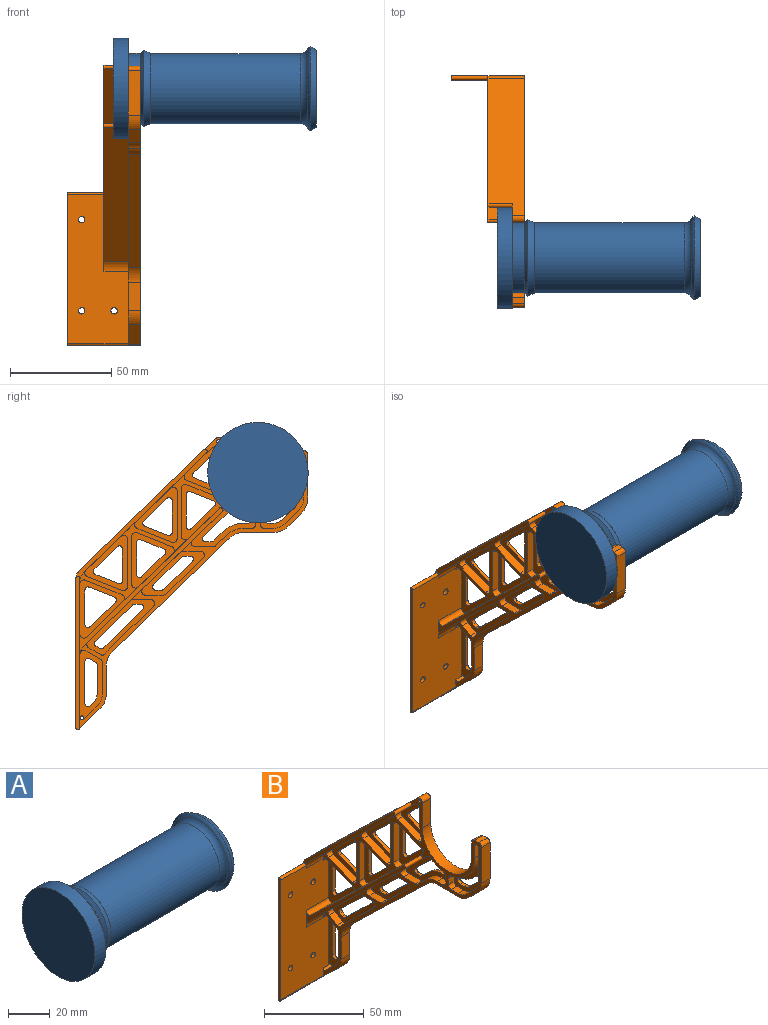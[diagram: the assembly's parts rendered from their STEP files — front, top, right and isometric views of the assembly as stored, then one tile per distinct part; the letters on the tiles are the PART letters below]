
ASSEMBLY  parts=2 mates=1
PART A: 12 faces, bbox 100.4x49.6x49.6 mm
  f0: cylinder r=17.3mm len=74.07mm, axis (-1,0,0), area 8051.5mm2, adj f1,f9
  f1: plane 34.94x34.94mm, normal (1,0,0), area 18.7mm2, adj f0,f10
  f2: cone r=17.3mm half-angle=45deg, axis (1,0,0), area 254.9mm2, adj f3,f10
  f3: cylinder r=17.3mm len=34.6mm, axis (-1,0,0), area 641.3mm2, adj f2,f4
  f4: plane 49.6x49.6mm, normal (1,0,0), area 992mm2, adj f3,f5
  f5: cylinder r=24.8mm len=49.6mm, axis (-1,0,0), area 1168.7mm2, adj f4,f6
  f6: plane 49.6x49.6mm, normal (-1,0,0), area 1932.2mm2, adj f5
  f7: plane 38.06x38.06mm, normal (1,0,0), area 1137.9mm2, adj f11
  f8: torus R=17.3mm, axis (-1,0,0), area 264.5mm2, adj f9,f11
  f9: torus R=21.3mm, axis (-1,0,0), area 473.5mm2, adj f0,f8
  f10: cone r=18.89mm half-angle=22.5deg, axis (-1,0,0), area 422.1mm2, adj f1,f2
  f11: cone r=20.76mm half-angle=30deg, axis (-1,0,0), area 433.1mm2, adj f7,f8
PART B: 211 faces, bbox 36x114.5x144.3 mm
  f0: plane 35.01x21.5mm, normal (-1,0,0), area 200.1mm2, adj f6,f11,f85,f86,f87,f88,f89,f96
  f1: plane 34.13x11.1mm, normal (-1,0,0), area 178.3mm2, adj f2,f28,f92,f93,f94,f95,f108,f122
  f2: cylinder r=7mm len=16mm, axis (1,0,0), area 69.8mm2, adj f1,f24,f25,f28,f36,f122
  f3: cylinder r=12mm len=4mm, axis (1,0,0), area 11.5mm2, adj f9,f10,f24,f124
  f4: plane 31.92x21.51mm, normal (-1,0,0), area 193.4mm2, adj f5,f25,f39,f82,f90,f91,f104,f105
  f5: plane 4.1x4mm, normal (0,0,1), area 16.4mm2, adj f4,f24,f90,f110
  f6: cylinder r=19.5mm len=19.31mm, axis (1,0,0), area 111.6mm2, adj f0,f11,f24,f112
  f7: plane 31x21.82mm, normal (-1,0,0), area 188.1mm2, adj f8,f25,f102,f103,f113,f114,f119,f120
  f8: plane 18.38x17.82mm, normal (0,0.7,0.72), area 102.4mm2, adj f7,f24,f114,f119
  f9: plane 33.53x27.62mm, normal (-1,0,0), area 210.3mm2, adj f3,f10,f25,f101,f107,f117,f118,f121
  f10: plane 21.68x21.02mm, normal (0,0.7,0.72), area 120.8mm2, adj f3,f9,f24,f118
  f11: plane 7.51x4mm, normal (0,-1,0), area 30mm2, adj f0,f6,f24,f96
  f12: plane 27.39x21.13mm, normal (-1,0,0), area 180.4mm2, adj f18,f53,f54,f75,f76,f77,f149,f150
  f13: plane 27.39x21.13mm, normal (-1,0,0), area 180.4mm2, adj f17,f50,f51,f70,f71,f72,f165,f166
  f14: plane 27.39x21.13mm, normal (-1,0,0), area 180.4mm2, adj f17,f48,f49,f67,f68,f69,f156,f157
  f15: plane 28.75x22.13mm, normal (-1,0,0), area 190mm2, adj f17,f28,f47,f63,f66,f84,f146,f147
  f16: plane 22.35x18.45mm, normal (-1,0,0), area 147.4mm2, adj f18,f40,f41,f52,f73,f74,f83,f168
  f17: plane 67.2x65.14mm, normal (0,0.7,0.72), area 1387.2mm2, adj f13,f14,f15,f24,f36,f66,f67,f69
  f18: plane 62.98x61.06mm, normal (0,-0.7,-0.72), area 1275.8mm2, adj f12,f16,f24,f29,f35,f62,f64,f74
  f19: plane 144.33x114.5mm, normal (1,0,0), area 3611.6mm2, adj f20,f21,f22,f23,f26,f34,f37,f38
  f20: plane 10.26x9.95mm, normal (0,-0.7,-0.72), area 85.8mm2, adj f19,f24,f57,f100
  f21: plane 6.65x6.45mm, normal (0,-0.7,-0.72), area 55.6mm2, adj f19,f24,f58,f61
  f22: plane 22.06x6mm, normal (0,-1,0), area 132.4mm2, adj f19,f24,f61,f79
  f23: plane 9.01x6mm, normal (0,1,0), area 54mm2, adj f19,f24,f38,f80
  f24: plane 144.05x112.8mm, normal (-1,0,0), area 1051mm2, adj f2,f3,f5,f6,f8,f10,f11,f17
  f25: plane 71.62x69.43mm, normal (0,-0.7,-0.72), area 1459.2mm2, adj f2,f4,f7,f9,f24,f36,f82,f98
  f26: plane 73.65x36mm, normal (0,1,0), area 2619.3mm2, adj f19,f27,f30,f31,f32,f33,f56,f99
  f27: plane 75.65x2mm, normal (-1,0,0), area 150.4mm2, adj f26,f28,f99,f100
  f28: plane 73.65x34mm, normal (0,-1,0), area 2254.3mm2, adj f1,f2,f15,f24,f27,f30,f31,f32
  f29: plane 27.39x21.13mm, normal (-1,0,0), area 180.4mm2, adj f18,f46,f55,f64,f65,f78,f125,f126
  f30: cylinder r=1.6mm len=3.2mm, axis (0,-1,0), area 20.1mm2, adj f26,f28
  f31: cylinder r=1.6mm len=3.2mm, axis (0,-1,0), area 20.1mm2, adj f26,f28
  f32: cylinder r=1.6mm len=3.2mm, axis (0,-1,0), area 20.1mm2, adj f26,f28
  f33: cylinder r=1.6mm len=3.2mm, axis (0,-1,0), area 20.1mm2, adj f26,f28
  f34: plane 67.59x65.52mm, normal (0,0.7,0.72), area 1597.4mm2, adj f19,f24,f35,f56,f81,f97
  f35: plane 65.46x65mm, normal (-1,0,0), area 179.4mm2, adj f18,f28,f34,f56,f62,f97,f99
  f36: plane 72.85x70.62mm, normal (-1,0,0), area 201.4mm2, adj f2,f17,f25,f28,f84,f98
  f37: plane 15.4x6mm, normal (0,-1,0), area 92.4mm2, adj f19,f24,f38,f81
  f38: cylinder r=17.5mm len=35mm, axis (1,0,0), area 329.9mm2, adj f19,f23,f24,f37
  f39: cylinder r=19.5mm len=8.95mm, axis (1,0,0), area 39.1mm2, adj f4,f24,f82,f109
  f40: plane 10.68x4mm, normal (0,1,0), area 42.7mm2, adj f16,f24,f41,f83
  f41: cylinder r=19.5mm len=6.96mm, axis (1,0,0), area 28.5mm2, adj f16,f24,f40,f73
  f42: plane 6x3mm, normal (0,0,1), area 18mm2, adj f19,f24,f79,f80
  f43: plane 13.89x6mm, normal (0,-1,0), area 83.3mm2, adj f19,f24,f57,f60
  f44: plane 14.95x6mm, normal (0,0,-1), area 89.7mm2, adj f19,f24,f58,f59
  f45: plane 57.9x56.13mm, normal (0,-0.7,-0.72), area 483.8mm2, adj f19,f24,f59,f60
  f46: plane 17.13x6.78mm, normal (0,-0.37,0.93), area 73.7mm2, adj f24,f29,f64,f65
  f47: plane 18.13x7.18mm, normal (0,0.37,-0.93), area 78mm2, adj f15,f24,f63,f66
  f48: plane 23.39x4mm, normal (0,-1,0), area 93.5mm2, adj f14,f24,f67,f68
  f49: plane 17.13x6.78mm, normal (0,0.37,-0.93), area 73.7mm2, adj f14,f24,f68,f69
  f50: plane 23.39x4mm, normal (0,-1,0), area 93.5mm2, adj f13,f24,f70,f71
  f51: plane 17.13x6.78mm, normal (0,0.37,-0.93), area 73.7mm2, adj f13,f24,f71,f72
  f52: plane 14.45x5.72mm, normal (0,-0.37,0.93), area 62.1mm2, adj f16,f24,f73,f74
  f53: plane 23.39x4mm, normal (0,1,0), area 93.5mm2, adj f12,f24,f75,f76
  f54: plane 17.13x6.78mm, normal (0,-0.37,0.93), area 73.7mm2, adj f12,f24,f76,f77
  f55: plane 23.39x4mm, normal (0,1,0), area 93.5mm2, adj f24,f29,f65,f78
  f56: cylinder r=5mm len=18mm, axis (-1,0,0), area 72.1mm2, adj f19,f26,f34,f35
  f57: cylinder r=10mm len=7.18mm, axis (-1,0,0), area 48.1mm2, adj f19,f20,f24,f43
  f58: cylinder r=10mm len=6.96mm, axis (1,0,0), area 46.2mm2, adj f19,f21,f24,f44
  f59: cylinder r=10mm len=6.96mm, axis (1,0,0), area 46.2mm2, adj f19,f24,f44,f45
  f60: cylinder r=10mm len=7.18mm, axis (1,0,0), area 48.1mm2, adj f19,f24,f43,f45
  f61: cylinder r=10mm len=7.18mm, axis (1,0,0), area 48.1mm2, adj f19,f21,f22,f24
  f62: cylinder r=7mm len=12mm, axis (-1,0,0), area 67.3mm2, adj f18,f24,f28,f35
  f63: cylinder r=2mm len=4mm, axis (1,0,0), area 15.6mm2, adj f15,f24,f28,f47
  f64: cylinder r=2mm len=4mm, axis (1,0,0), area 16mm2, adj f18,f24,f29,f46
  f65: cylinder r=2mm len=4mm, axis (-1,0,0), area 15.6mm2, adj f24,f29,f46,f55
  f66: cylinder r=2mm len=4mm, axis (1,0,0), area 16mm2, adj f15,f17,f24,f47
  f67: cylinder r=2mm len=4mm, axis (1,0,0), area 18.7mm2, adj f14,f17,f24,f48
  f68: cylinder r=2mm len=4mm, axis (-1,0,0), area 15.6mm2, adj f14,f24,f48,f49
  f69: cylinder r=2mm len=4mm, axis (1,0,0), area 16mm2, adj f14,f17,f24,f49
  f70: cylinder r=2mm len=4mm, axis (1,0,0), area 18.7mm2, adj f13,f17,f24,f50
  f71: cylinder r=2mm len=4mm, axis (-1,0,0), area 15.6mm2, adj f13,f24,f50,f51
  f72: cylinder r=2mm len=4mm, axis (1,0,0), area 16mm2, adj f13,f17,f24,f51
  f73: cylinder r=2mm len=4mm, axis (1,0,0), area 18.5mm2, adj f16,f24,f41,f52
  f74: cylinder r=2mm len=4mm, axis (-1,0,0), area 16mm2, adj f16,f18,f24,f52
  f75: cylinder r=2mm len=4mm, axis (-1,0,0), area 18.7mm2, adj f12,f18,f24,f53
  f76: cylinder r=2mm len=4mm, axis (-1,0,0), area 15.6mm2, adj f12,f24,f53,f54
  f77: cylinder r=2mm len=4mm, axis (-1,0,0), area 16mm2, adj f12,f18,f24,f54
  f78: cylinder r=2mm len=4mm, axis (-1,0,0), area 18.7mm2, adj f18,f24,f29,f55
  f79: cylinder r=2mm len=6mm, axis (-1,0,0), area 18.8mm2, adj f19,f22,f24,f42
  f80: cylinder r=2mm len=6mm, axis (1,0,0), area 18.8mm2, adj f19,f23,f24,f42
  f81: cylinder r=2mm len=6mm, axis (-1,0,0), area 28.1mm2, adj f19,f24,f34,f37
  f82: cylinder r=2mm len=4mm, axis (1,0,0), area 11.3mm2, adj f4,f24,f25,f39
  f83: cylinder r=2mm len=4mm, axis (-1,0,0), area 18.7mm2, adj f16,f18,f24,f40
  f84: cylinder r=2mm len=16mm, axis (-1,0,0), area 74.9mm2, adj f15,f17,f28,f36
  f85: plane 20.56x4mm, normal (0,1,0), area 82.2mm2, adj f0,f24,f86,f96
  f86: cylinder r=8mm len=5.74mm, axis (1,0,0), area 25.6mm2, adj f0,f24,f85,f87
  f87: plane 6.65x6.45mm, normal (0,0.7,0.72), area 37mm2, adj f0,f24,f86,f88
  f88: cylinder r=8mm len=5.57mm, axis (1,0,0), area 24.6mm2, adj f0,f24,f87,f89
  f89: plane 4.85x4mm, normal (0,0,1), area 19.4mm2, adj f0,f24,f88,f111
  f90: cylinder r=12mm len=8.35mm, axis (1,0,0), area 37mm2, adj f4,f5,f24,f91
  f91: plane 5.45x5.29mm, normal (0,0.7,0.72), area 30.4mm2, adj f4,f24,f90,f115
  f92: cylinder r=12mm len=4mm, axis (1,0,0), area 5.9mm2, adj f1,f24,f93,f123
  f93: plane 13.89x4mm, normal (0,1,0), area 55.5mm2, adj f1,f24,f92,f94
  f94: cylinder r=8mm len=5.74mm, axis (1,0,0), area 25.6mm2, adj f1,f24,f93,f95
  f95: plane 6.87x6.66mm, normal (0,0.7,0.72), area 38.3mm2, adj f1,f24,f94,f209
  f96: cylinder r=1.5mm len=6mm, axis (1,0,0), area 37.7mm2, adj f0,f11,f19,f24,f85
  f97: cylinder r=1mm len=12mm, axis (-1,0,0), area 37.7mm2, adj f18,f24,f34,f35
  f98: cylinder r=1mm len=12mm, axis (-1,0,0), area 37.7mm2, adj f17,f24,f25,f36
  f99: cylinder r=1mm len=18mm, axis (-1,0,0), area 56.5mm2, adj f26,f27,f28,f35
  f100: cylinder r=1mm len=36mm, axis (1,0,0), area 108.3mm2, adj f19,f20,f24,f26,f27,f28
  f101: plane 8.62x4mm, normal (0,0,-1), area 34.5mm2, adj f9,f24,f117,f118
  f102: plane 8.62x4mm, normal (0,0,1), area 34.5mm2, adj f7,f24,f119,f120
  f103: plane 8.62x4mm, normal (0,0,-1), area 34.5mm2, adj f7,f24,f113,f114
  f104: plane 8.62x4mm, normal (0,0,1), area 34.5mm2, adj f4,f24,f115,f116
  f105: plane 4.21x4mm, normal (0,1,0), area 16.8mm2, adj f4,f24,f109,f110
  f106: plane 4.21x4mm, normal (0,-1,0), area 16.8mm2, adj f0,f24,f111,f112
  f107: plane 5.74x4mm, normal (0,-0.5,0.86), area 26.6mm2, adj f9,f24,f121,f124
  f108: plane 7.08x4.13mm, normal (0,0.5,-0.86), area 32.8mm2, adj f1,f24,f122,f123
  f109: cylinder r=2mm len=4mm, axis (1,0,0), area 11.4mm2, adj f4,f24,f39,f105
  f110: cylinder r=2mm len=4mm, axis (1,0,0), area 12.6mm2, adj f4,f5,f24,f105
  f111: cylinder r=2mm len=4mm, axis (-1,0,0), area 12.6mm2, adj f0,f24,f89,f106
  f112: cylinder r=2mm len=4mm, axis (1,0,0), area 11.4mm2, adj f0,f6,f24,f106
  f113: cylinder r=2mm len=4mm, axis (-1,0,0), area 6.2mm2, adj f7,f24,f25,f103
  f114: cylinder r=2mm len=4mm, axis (1,0,0), area 19mm2, adj f7,f8,f24,f103
  f115: cylinder r=2mm len=4mm, axis (-1,0,0), area 6.2mm2, adj f4,f24,f91,f104
  f116: cylinder r=2mm len=4mm, axis (1,0,0), area 19mm2, adj f4,f24,f25,f104
  f117: cylinder r=2mm len=4mm, axis (-1,0,0), area 6.2mm2, adj f9,f24,f25,f101
  f118: cylinder r=2mm len=4mm, axis (1,0,0), area 19mm2, adj f9,f10,f24,f101
  f119: cylinder r=2mm len=4mm, axis (-1,0,0), area 6.2mm2, adj f7,f8,f24,f102
  f120: cylinder r=2mm len=4mm, axis (1,0,0), area 19mm2, adj f7,f24,f25,f102
  f121: cylinder r=2mm len=4mm, axis (1,0,0), area 14.7mm2, adj f9,f24,f25,f107
  f122: cylinder r=2mm len=4mm, axis (1,0,0), area 16.1mm2, adj f1,f2,f24,f108
  f123: cylinder r=2mm len=4mm, axis (1,0,0), area 9.3mm2, adj f1,f24,f92,f108
  f124: cylinder r=2mm len=4mm, axis (1,0,0), area 12.3mm2, adj f3,f9,f24,f107
  f125: plane 11.51x11.16mm, normal (0,-0.7,-0.72), area 32.1mm2, adj f19,f29,f200,f202
  f126: plane 11.51x4.56mm, normal (0,-0.37,0.93), area 24.8mm2, adj f19,f29,f200,f201
  f127: plane 15.72x2mm, normal (0,1,0), area 31.4mm2, adj f19,f29,f201,f202
  f128: plane 2x0.54mm, normal (0,1,0), area 1.1mm2, adj f4,f19,f188,f192
  f129: cylinder r=22mm len=7.16mm, axis (-1,0,0), area 15.6mm2, adj f4,f19,f188,f189
  f130: plane 13.34x12.93mm, normal (0,-0.7,-0.72), area 37.1mm2, adj f4,f19,f189,f190
  f131: plane 2.87x2mm, normal (0,0,1), area 5.7mm2, adj f4,f19,f190,f191
  f132: plane 4.87x4.72mm, normal (0,0.7,0.72), area 13.6mm2, adj f4,f19,f133,f191
  f133: cylinder r=14.5mm len=10.09mm, axis (-1,0,0), area 22.3mm2, adj f4,f19,f132,f134
  f134: plane 2.1x2mm, normal (0,0,1), area 4.2mm2, adj f4,f19,f133,f192
  f135: plane 2.87x2mm, normal (0,0,-1), area 5.7mm2, adj f9,f19,f184,f187
  f136: plane 18.43x17.87mm, normal (0,-0.7,-0.72), area 51.3mm2, adj f9,f19,f184,f185
  f137: plane 2x1.89mm, normal (0,-0.5,0.86), area 4.4mm2, adj f9,f19,f185,f186
  f138: cylinder r=14.5mm len=2mm, axis (-1,0,0), area 3.4mm2, adj f9,f19,f139,f186
  f139: plane 18.14x17.59mm, normal (0,0.7,0.72), area 50.5mm2, adj f9,f19,f138,f187
  f140: plane 3.01x2mm, normal (0,0.5,-0.86), area 7mm2, adj f1,f19,f181,f183
  f141: plane 20.86x2mm, normal (0,-1,0), area 41.7mm2, adj f1,f19,f181,f182
  f142: plane 2x1.78mm, normal (0,0.7,0.72), area 5mm2, adj f1,f19,f143,f182
  f143: cylinder r=5.5mm len=3.95mm, axis (-1,0,0), area 8.8mm2, adj f1,f19,f142,f144
  f144: plane 13.89x2mm, normal (0,1,0), area 27.8mm2, adj f1,f19,f143,f145
  f145: cylinder r=14.5mm len=2mm, axis (-1,0,0), area 1.1mm2, adj f1,f19,f144,f183
  f146: plane 12.51x4.95mm, normal (0,0.37,-0.93), area 26.9mm2, adj f15,f19,f178,f180
  f147: plane 17.09x2mm, normal (0,-1,0), area 34.2mm2, adj f15,f19,f178,f179
  f148: plane 12.51x12.13mm, normal (0,0.7,0.72), area 34.9mm2, adj f15,f19,f179,f180
  f149: plane 15.72x2mm, normal (0,1,0), area 31.4mm2, adj f12,f19,f203,f205
  f150: plane 11.51x11.16mm, normal (0,-0.7,-0.72), area 32.1mm2, adj f12,f19,f203,f204
  f151: plane 11.51x4.56mm, normal (0,-0.37,0.93), area 24.8mm2, adj f12,f19,f204,f205
  f152: plane 2.87x2mm, normal (0,0,-1), area 5.7mm2, adj f7,f19,f193,f196
  f153: plane 14.26x13.82mm, normal (0,-0.7,-0.72), area 39.7mm2, adj f7,f19,f193,f194
  f154: plane 2.87x2mm, normal (0,0,1), area 5.7mm2, adj f7,f19,f194,f195
  f155: plane 14.26x13.82mm, normal (0,0.7,0.72), area 39.7mm2, adj f7,f19,f195,f196
  f156: plane 15.72x2mm, normal (0,-1,0), area 31.4mm2, adj f14,f19,f197,f199
  f157: plane 11.51x11.16mm, normal (0,0.7,0.72), area 32.1mm2, adj f14,f19,f197,f198
  f158: plane 11.51x4.56mm, normal (0,0.37,-0.93), area 24.8mm2, adj f14,f19,f198,f199
  f159: plane 2x0.54mm, normal (0,-1,0), area 1.1mm2, adj f0,f19,f175,f177
  f160: plane 2.85x2mm, normal (0,0,1), area 5.7mm2, adj f0,f19,f161,f175
  f161: cylinder r=5.5mm len=3.83mm, axis (-1,0,0), area 8.5mm2, adj f0,f19,f160,f162
  f162: plane 6.65x6.45mm, normal (0,0.7,0.72), area 18.5mm2, adj f0,f19,f161,f163
  f163: cylinder r=5.5mm len=2mm, axis (-1,0,0), area 1.6mm2, adj f0,f19,f162,f176
  f164: cylinder r=22mm len=11.87mm, axis (-1,0,0), area 28mm2, adj f0,f19,f176,f177
  f165: plane 15.72x2mm, normal (0,-1,0), area 31.4mm2, adj f13,f19,f172,f174
  f166: plane 11.51x11.16mm, normal (0,0.7,0.72), area 32.1mm2, adj f13,f19,f172,f173
  f167: plane 11.51x4.56mm, normal (0,0.37,-0.93), area 24.8mm2, adj f13,f19,f173,f174
  f168: plane 7.82x3.09mm, normal (0,-0.37,0.93), area 16.8mm2, adj f16,f19,f206,f208
  f169: cylinder r=22mm len=4.05mm, axis (-1,0,0), area 8.1mm2, adj f16,f19,f170,f206
  f170: plane 5.95x2mm, normal (0,1,0), area 11.9mm2, adj f16,f19,f169,f207
  f171: plane 7.41x7.19mm, normal (0,-0.7,-0.72), area 20.7mm2, adj f16,f19,f207,f208
  f172: cylinder r=1.5mm len=2.54mm, axis (1,0,0), area 7mm2, adj f13,f19,f165,f166
  f173: cylinder r=1.5mm len=2.47mm, axis (1,0,0), area 6mm2, adj f13,f19,f166,f167
  f174: cylinder r=1.5mm len=2.05mm, axis (1,0,0), area 5.8mm2, adj f13,f19,f165,f167
  f175: cylinder r=1.5mm len=2mm, axis (1,0,0), area 4.7mm2, adj f0,f19,f159,f160
  f176: cylinder r=1.5mm len=2.63mm, axis (-1,0,0), area 9.2mm2, adj f0,f19,f163,f164
  f177: cylinder r=1.5mm len=2mm, axis (-1,0,0), area 4.1mm2, adj f0,f19,f159,f164
  f178: cylinder r=1.5mm len=2.05mm, axis (1,0,0), area 5.8mm2, adj f15,f19,f146,f147
  f179: cylinder r=1.5mm len=2.54mm, axis (1,0,0), area 7mm2, adj f15,f19,f147,f148
  f180: cylinder r=1.5mm len=2.47mm, axis (1,0,0), area 6mm2, adj f15,f19,f146,f148
  f181: cylinder r=1.5mm len=2.26mm, axis (1,0,0), area 6.3mm2, adj f1,f19,f140,f141
  f182: cylinder r=1.5mm len=2.54mm, axis (1,0,0), area 7mm2, adj f1,f19,f141,f142
  f183: cylinder r=1.5mm len=2mm, axis (-1,0,0), area 3.2mm2, adj f1,f19,f140,f145
  f184: cylinder r=1.5mm len=2mm, axis (1,0,0), area 2.3mm2, adj f9,f19,f135,f136
  f185: cylinder r=1.5mm len=2.37mm, axis (1,0,0), area 5.5mm2, adj f9,f19,f136,f137
  f186: cylinder r=1.5mm len=2mm, axis (-1,0,0), area 4.2mm2, adj f9,f19,f137,f138
  f187: cylinder r=1.5mm len=2.58mm, axis (1,0,0), area 7.1mm2, adj f9,f19,f135,f139
  f188: cylinder r=1.5mm len=2mm, axis (-1,0,0), area 4.1mm2, adj f4,f19,f128,f129
  f189: cylinder r=1.5mm len=2mm, axis (-1,0,0), area 4mm2, adj f4,f19,f129,f130
  f190: cylinder r=1.5mm len=2.58mm, axis (1,0,0), area 7.1mm2, adj f4,f19,f130,f131
  f191: cylinder r=1.5mm len=2mm, axis (1,0,0), area 2.3mm2, adj f4,f19,f131,f132
  f192: cylinder r=1.5mm len=2mm, axis (1,0,0), area 4.7mm2, adj f4,f19,f128,f134
  f193: cylinder r=1.5mm len=2mm, axis (1,0,0), area 2.3mm2, adj f7,f19,f152,f153
  f194: cylinder r=1.5mm len=2.58mm, axis (1,0,0), area 7.1mm2, adj f7,f19,f153,f154
  f195: cylinder r=1.5mm len=2mm, axis (1,0,0), area 2.3mm2, adj f7,f19,f154,f155
  f196: cylinder r=1.5mm len=2.58mm, axis (1,0,0), area 7.1mm2, adj f7,f19,f152,f155
  f197: cylinder r=1.5mm len=2.54mm, axis (1,0,0), area 7mm2, adj f14,f19,f156,f157
  f198: cylinder r=1.5mm len=2.47mm, axis (1,0,0), area 6mm2, adj f14,f19,f157,f158
  f199: cylinder r=1.5mm len=2.05mm, axis (1,0,0), area 5.8mm2, adj f14,f19,f156,f158
  f200: cylinder r=1.5mm len=2.47mm, axis (1,0,0), area 6mm2, adj f19,f29,f125,f126
  f201: cylinder r=1.5mm len=2.05mm, axis (1,0,0), area 5.8mm2, adj f19,f29,f126,f127
  f202: cylinder r=1.5mm len=2.54mm, axis (1,0,0), area 7mm2, adj f19,f29,f125,f127
  f203: cylinder r=1.5mm len=2.54mm, axis (1,0,0), area 7mm2, adj f12,f19,f149,f150
  f204: cylinder r=1.5mm len=2.47mm, axis (1,0,0), area 6mm2, adj f12,f19,f150,f151
  f205: cylinder r=1.5mm len=2.05mm, axis (1,0,0), area 5.8mm2, adj f12,f19,f149,f151
  f206: cylinder r=1.5mm len=2.05mm, axis (-1,0,0), area 6.4mm2, adj f16,f19,f168,f169
  f207: cylinder r=1.5mm len=2.54mm, axis (1,0,0), area 7mm2, adj f16,f19,f170,f171
  f208: cylinder r=1.5mm len=2.47mm, axis (1,0,0), area 6mm2, adj f16,f19,f168,f171
  f209: cylinder r=1mm len=6mm, axis (1,0,0), area 21.9mm2, adj f1,f19,f24,f28,f95
  f210: cylinder r=1mm len=6mm, axis (-1,0,0), area 37.7mm2, adj f19,f24
PLACE A rot(axis=(-1,0,0),171.6deg) t=(7.88,-4.42,277.17)mm
PLACE B t=(7.63,0,0)mm fixed
MATE pin_slot A.f0 <-> B.f6  axis (-1,0,0) through (74.63,8,138.75)mm
